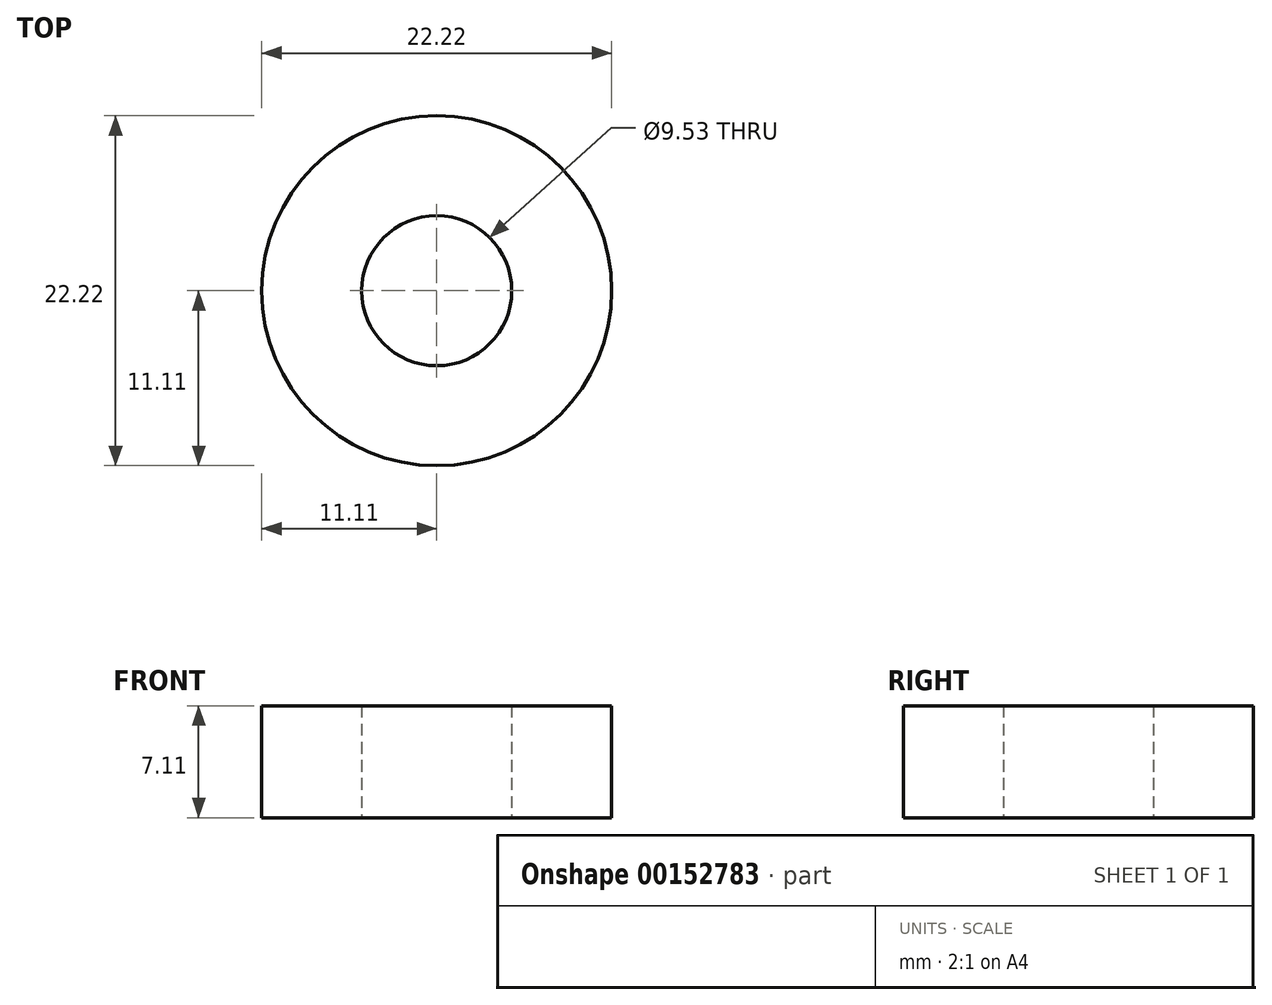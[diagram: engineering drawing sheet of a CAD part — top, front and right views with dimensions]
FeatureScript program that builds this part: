
annotation { "Feature Type Name" : "Feature", "Feature Type Description" : "" }
export const myFeature = defineFeature(function(context is Context, id is Id, definition is map)
    precondition{}
    {
        {
            var Q0;
            Q0=qCreatedBy(makeId("Top.planeOp"),FACE);
            var sketch = newSketch(context, id + "F0", { "sketchPlane" : qUnion([Q0])});
            skCircle(sketch, "E0", {"center": v(0, 0) * mm, "radius": 4.76 * mm});
            skCircle(sketch, "E1", {"center": v(0, 0) * mm, "radius": 11.11 * mm});
            skSolve(sketch);
        }
        {
            var Q0;
            Q0 = qSketchRegion(id + "F0", true);
            extrude(context, id + "F1", {"entities" : qUnion([Q0]), "depth" : 7.11 * mm});
        }
    });
